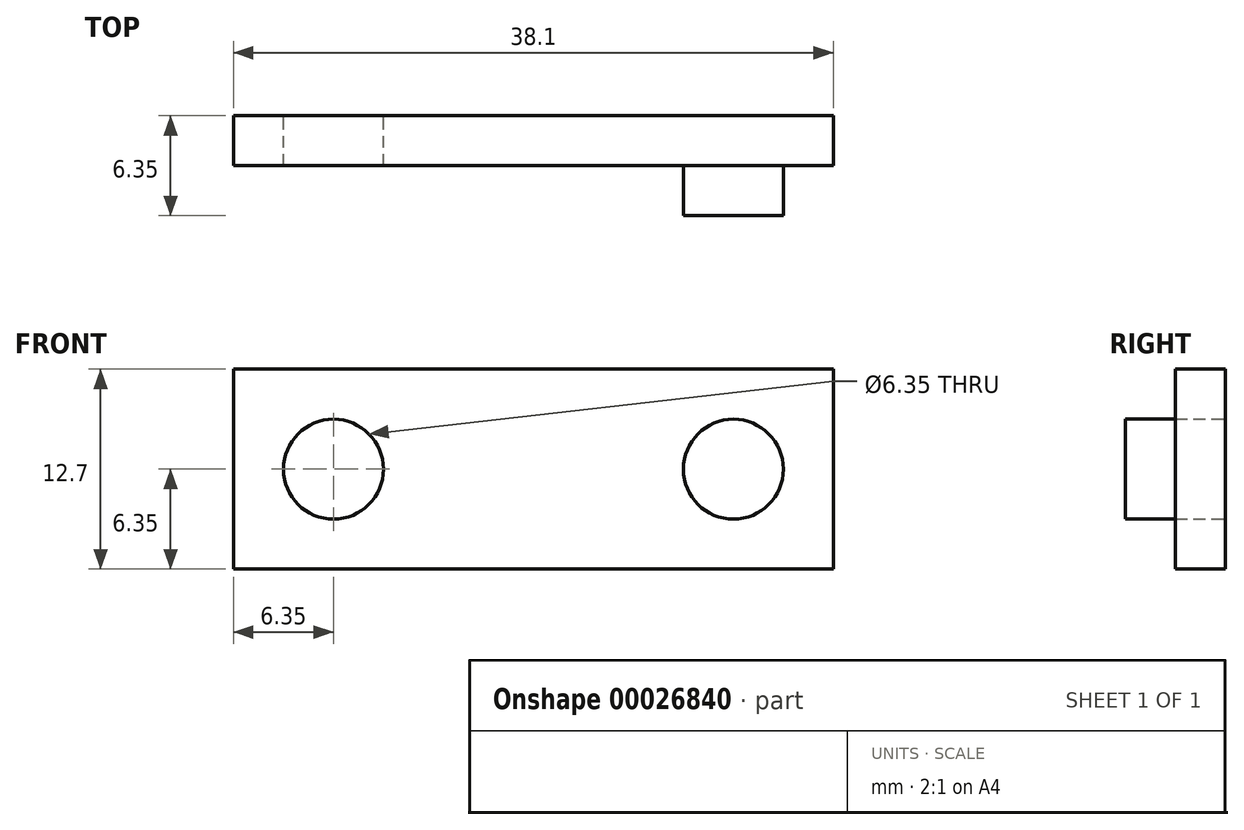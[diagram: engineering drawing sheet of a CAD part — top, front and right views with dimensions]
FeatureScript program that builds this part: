
annotation { "Feature Type Name" : "Feature", "Feature Type Description" : "" }
export const myFeature = defineFeature(function(context is Context, id is Id, definition is map)
    precondition{}
    {
        {
            var Q0;
            Q0=qCreatedBy(makeId("Front.planeOp"),FACE);
            var sketch = newSketch(context, id + "F0", { "sketchPlane" : qUnion([Q0])});
            skLineSegment(sketch, "E0.bottom", {"start": v(0, 0) * mm, "end": v(38.1, 0) * mm});
            skLineSegment(sketch, "E0.top", {"start": v(0, 12.7) * mm, "end": v(38.1, 12.7) * mm});
            skLineSegment(sketch, "E0.left", {"start": v(0, 0) * mm, "end": v(0, 12.7) * mm});
            skLineSegment(sketch, "E0.right", {"start": v(38.1, 0) * mm, "end": v(38.1, 12.7) * mm});
            skPoint(sketch, "E1", {"position": v(0, 6.35) * mm});
            skPoint(sketch, "E2", {"position": v(6.35, 6.35) * mm});
            skCircle(sketch, "E3", {"center": v(6.35, 6.35) * mm, "radius": 3.18 * mm});
            skPoint(sketch, "E4", {"position": v(38.1, 6.35) * mm});
            skPoint(sketch, "E5", {"position": v(31.75, 6.35) * mm});
            skCircle(sketch, "E6", {"center": v(31.75, 6.35) * mm, "radius": 3.18 * mm});
            skSolve(sketch);
        }
        {
            var Q0;
            Q0=makeQuery(id+"F0.imprint","IMPRINT",FACE,{"disambiguationData":[TD([[makeQuery(id+"F0.imprint","IMPRINT",EDGE,{"derivedFrom":sQuery(id+"F0.wireOp",EDGE,"E0.bottom")}),1.0]])]});
            extrude(context, id + "F1", {"entities" : qUnion([Q0]), "depth" : 3.17 * mm});
        }
        {
            var Q0;
            Q0=makeQuery(id+"F0.imprint","IMPRINT",FACE,{"disambiguationData":[TD([[makeQuery(id+"F0.imprint","IMPRINT",EDGE,{"derivedFrom":sQuery(id+"F0.wireOp",EDGE,"E6")}),1.0]])]});
            extrude(context, id + "F2", {"entities" : qUnion([Q0]), "operationType" : NewBodyOperationType.ADD, "depth" : 6.35 * mm});
        }
    });
